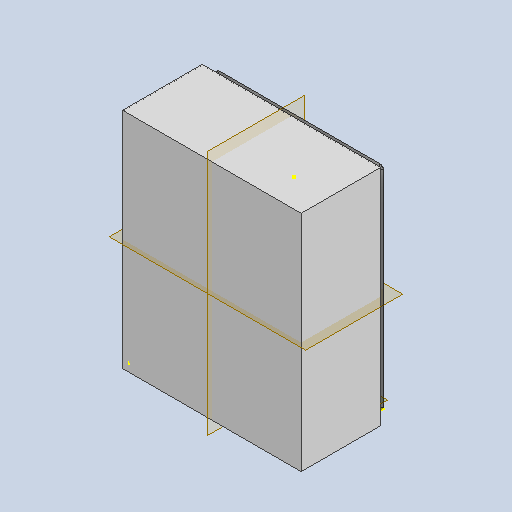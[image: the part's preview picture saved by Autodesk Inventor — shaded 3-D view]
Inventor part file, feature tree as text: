
AUTODESK INVENTOR PART (.ipt)
format: ipt  version: 2023 (Build 270158030, 158C)  size: 364,032 bytes
history: native  units: mm
features: sketch x9, other x8, extrude x7, projected_geometry x6, loft x4, plane x3, mirror x2, fillet x2, pattern_linear x1
ambient origin geometry x8: Origin, YZ Plane, XZ Plane, XY Plane, X Axis, Y Axis, Z Axis, Center Point
bodies: Solid1 (feature_tree)
feature tree (42):
  extrude  "Extrusion1"  Depth=495.0mm
  extrude  "Extrusion2"  Depth=1.6mm
  extrude  "Extrusion3"  Depth=18.9mm
  extrude  "Extrusion4"  Depth=1.6mm
  extrude  "Extrusion5"  Depth=6.0mm
  extrude  "Extrusion6"  Depth=13.0mm TaperAngle=0.0deg
  plane  "Work Plane3"
  plane  "Work Plane4"
  mirror  "Mirror1"
  mirror  "Mirror2"
  sketch  "Sketch8"  dims[d21=45.0deg d22=6.0mm]
  sketch  "Sketch9"  dims[d23=10.0mm d24=0.0mm d25=0.0mm d26=90.0deg]
  loft  "Loft1"
  loft  "Loft2"
  loft  "Loft3"
  loft  "Loft4"
  fillet  "Fillet2"  [1 undecoded]
  plane  "Work Plane5"
  extrude  "Extrusion7"  TaperAngle=0.0deg  [1 undecoded]
  pattern_linear  "Rectangular Pattern1"  Spacing1=0.0mm  [1 undecoded]
  fillet  "Fillet1"  [1 undecoded]
  sketch  "Sketch1"  dims[d0=395.0mm d1=495.0mm]
  sketch  "Sketch2"  dims[d6=1.6mm d7=0.0mm d8=1.6mm]
  projected_geometry  "Projected Loop1"
  sketch  "Sketch3"  dims[d9=173.0mm d10=0.0mm d11=18.9mm]
  projected_geometry  "Projected Loop2"
  sketch  "Sketch4"  dims[d12=1.6mm d13=0.0mm d14=1.6mm]
  projected_geometry  "Projected Loop3"
  sketch  "Sketch6"  dims[d15=13.0mm d16=0.0mm d17=6.0mm]
  sketch  "Sketch7"  dims[d18=45.0deg d19=13.0mm d20=0.0mm]
  projected_geometry  "Projected Loop4"
  projected_geometry  "Projected Loop5"
  projected_geometry  "Projected Loop6"
  other  "Edges1"
  other  "Edges2"
  other  "Edges3"
  other  "Edges4"
  other  "Edges5"
  other  "Edges6"
  other  "Edges7"
  other  "Edges8"
  sketch  "Sketch10"  dims[d27=0.0mm d28=90.0deg d29=8.0mm d30=0.0mm d31=90.0deg d32=0.0mm d33=90.0deg d34=0.0mm d35=90.0deg d36=0.0mm d37=90.0deg d38=0.0mm d39=90.0deg d40=0.0mm d41=90.0deg d42=8.0mm d43=-25.0mm d44=0.8mm d45=0.8mm d46=1.0mm d47=0.8mm d48=0.8mm d49=4.3mm d50=22.68928mm d51=13.0mm d52=7.0mm d53=2.069249mm d54=10.0mm d55=0.0mm d56=20.0mm d58=390.0mm d2=0.5mm d3=0.872665mm]
note: 4 required parameter values undecoded (feature->parameter linkage not recoverable at this tier; creation-order binding heuristic only, values carry confidence <= 0.55)
